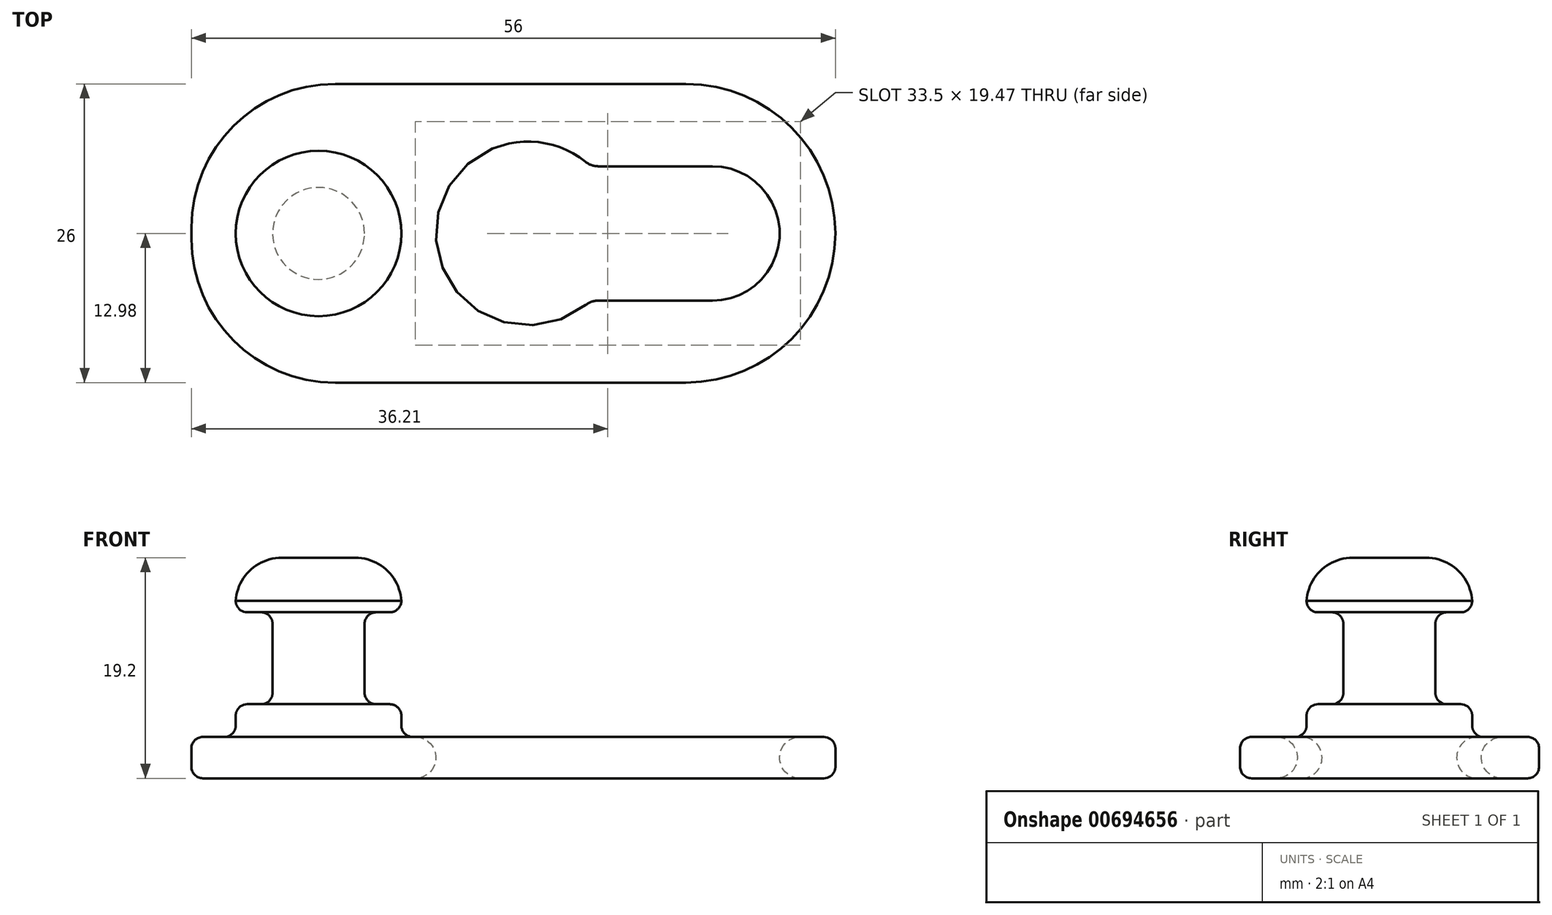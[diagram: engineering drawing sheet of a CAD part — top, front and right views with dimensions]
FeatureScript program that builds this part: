
annotation { "Feature Type Name" : "Feature", "Feature Type Description" : "" }
export const myFeature = defineFeature(function(context is Context, id is Id, definition is map)
    precondition{}
    {
        {
            var Q0;
            Q0=qCreatedBy(makeId("Top.planeOp"),FACE);
            var sketch = newSketch(context, id + "F0", { "sketchPlane" : qUnion([Q0])});
            skLineSegment(sketch, "E0", {"start": v(0, 52.84) * mm, "end": v(0, -52.67) * mm, "construction": true});
            skLineSegment(sketch, "E1", {"start": v(-57.06, 0) * mm, "end": v(21.4, 0) * mm, "construction": true});
            skLineSegment(sketch, "E2.0", {"start": v(-29.76, 0.52) * mm, "end": v(-29.76, 0) * mm});
            skLineSegment(sketch, "E3.0", {"start": v(-17.26, -12.98) * mm, "end": v(13.24, -12.98) * mm});
            skLineSegment(sketch, "E4.0", {"start": v(-17.26, 13.02) * mm, "end": v(13.24, 13.02) * mm});
            skLineSegment(sketch, "E5.0", {"start": v(5.4, 5.9) * mm, "end": v(5.4, 5.85) * mm});
            skArc(sketch, "E6", {"start": v(4.96, 5.85) * mm, "mid": v(-8.5, 0) * mm, "end": v(4.96, -5.85) * mm});
            skArc(sketch, "E7", {"start": v(15.55, -5.85) * mm, "mid": v(21.4, 0) * mm, "end": v(15.55, 5.85) * mm});
            skLineSegment(sketch, "E8", {"start": v(15.55, 5.85) * mm, "end": v(4.9, 5.85) * mm});
            skLineSegment(sketch, "E9", {"start": v(15.55, -5.85) * mm, "end": v(4.9, -5.85) * mm});
            skLineSegment(sketch, "E10.trimOffspring", {"start": v(5.4, -5.85) * mm, "end": v(5.4, -5.9) * mm});
            skPoint(sketch, "E11.0.start.orphan", {"position": v(16.05, 13) * mm});
            skPoint(sketch, "E12.trimOffspring.end.orphan", {"position": v(16.05, -13) * mm});
            skCircle(sketch, "E13", {"center": v(-18.76, 0) * mm, "radius": 7.2 * mm});
            skLineSegment(sketch, "E14", {"start": v(-11.56, 0) * mm, "end": v(-11.56, -14.31) * mm, "construction": true});
            skLineSegment(sketch, "E15", {"start": v(-25.96, 0) * mm, "end": v(-25.96, -14.7) * mm, "construction": true});
            skLineSegment(sketch, "E16", {"start": v(21.4, 0) * mm, "end": v(46.22, 0) * mm, "construction": true});
            skLineSegment(sketch, "E17", {"start": v(-8.5, 0) * mm, "end": v(-8.5, -14.52) * mm, "construction": true});
            skPoint(sketch, "E18.visualSharp", {"position": v(-29.06, 13) * mm});
            skArc(sketch, "E18.filletArc", {"start": v(-17.26, 13.02) * mm, "mid": v(-26.1, 9.36) * mm, "end": v(-29.76, 0.52) * mm});
            skArc(sketch, "E19.filletArc", {"start": v(-29.76, -0.48) * mm, "mid": v(-26.1, -9.32) * mm, "end": v(-17.26, -12.98) * mm});
            skPoint(sketch, "E20.visualSharp", {"position": v(26.94, 13) * mm});
            skArc(sketch, "E20.filletArc", {"start": v(26.24, 0.02) * mm, "mid": v(22.44, 9.21) * mm, "end": v(13.24, 13.02) * mm});
            skArc(sketch, "E21.filletArc", {"start": v(13.24, -12.98) * mm, "mid": v(22.44, -9.17) * mm, "end": v(26.24, 0.02) * mm});
            skLineSegment(sketch, "E22", {"start": v(-29.76, 0) * mm, "end": v(-29.76, -0.48) * mm});
            skSolve(sketch);
        }
        {
            var Q0;
            Q0=makeQuery(id+"F0.imprint","IMPRINT",FACE,{"disambiguationData":[TD([[makeQuery(id+"F0.imprint","IMPRINT",EDGE,{"derivedFrom":sQuery(id+"F0.wireOp",EDGE,"E2.0")}),1.0]])]});
            var Q1;
            Q1=makeQuery(id+"F0.imprint","IMPRINT",FACE,{"disambiguationData":[TD([[makeQuery(id+"F0.imprint","IMPRINT",EDGE,{"derivedFrom":sQuery(id+"F0.wireOp",EDGE,"E13")}),1.0]])]});
            extrude(context, id + "F1", {"entities" : qUnion([Q0, Q1]), "depth" : 3.6 * mm, "offsetDistance" : 25 * mm});
        }
        {
            var Q0;
            Q0=makeQuery(id+"F1.opExtrude","SWEPT_FACE",FACE,{"disambiguationData":[OSD([sQuery(id+"F0.wireOp",EDGE,"E6")])]});
            var Q1;
            Q1=makeQuery(id+"F1.opExtrude","SWEPT_FACE",FACE,{"disambiguationData":[OSD([sQuery(id+"F0.wireOp",EDGE,"E8")])]});
            var Q2;
            Q2=makeQuery(id+"F1.opExtrude","SWEPT_FACE",FACE,{"disambiguationData":[OSD([sQuery(id+"F0.wireOp",EDGE,"E7")])]});
            var Q3;
            Q3=makeQuery(id+"F1.opExtrude","SWEPT_FACE",FACE,{"disambiguationData":[OSD([sQuery(id+"F0.wireOp",EDGE,"E9")])]});
            fillet(context, id + "F2", {"entities" : qUnion([Q0, Q1, Q2, Q3]), "radius" : 1.8 * mm, "tangentPropagation" : true, "allowEdgeOverflow" : false});
        }
        {
            var Q0;
            Q0=qCreatedBy(makeId("Top.planeOp"),FACE);
            var sketch = newSketch(context, id + "F3", { "sketchPlane" : qUnion([Q0])});
            skCircle(sketch, "E23", {"center": v(-18.7, 0) * mm, "radius": 7.2 * mm});
            skSolve(sketch);
        }
        {
            var Q0;
            Q0 = qSketchRegion(id + "F3", true);
            extrude(context, id + "F4", {"entities" : qUnion([Q0]), "operationType" : NewBodyOperationType.ADD, "depth" : 6.45 * mm, "offsetDistance" : 25 * mm});
        }
        {
            var Q0;
            Q0=makeQuery(id+"F4.opExtrude","CAP_FACE",FACE,{"disambiguationData":[OSD([sQuery(id+"F3.wireOp",EDGE,"E23")])],"isStart":false});
            var sketch = newSketch(context, id + "F5", { "sketchPlane" : qUnion([Q0])});
            skCircle(sketch, "E24", {"center": v(-18.7, 0) * mm, "radius": 4 * mm});
            skSolve(sketch);
        }
        {
            var Q0;
            Q0=makeQuery(id+"F5.imprint","IMPRINT",FACE,{"disambiguationData":[TD([[makeQuery(id+"F5.imprint","IMPRINT",EDGE,{"derivedFrom":sQuery(id+"F5.wireOp",EDGE,"E24")}),1.0]])]});
            extrude(context, id + "F6", {"entities" : qUnion([Q0]), "operationType" : NewBodyOperationType.ADD, "depth" : 8 * mm, "offsetDistance" : 25 * mm});
        }
        {
            var Q0;
            Q0=makeQuery(id+"F6.opExtrude","CAP_FACE",FACE,{"disambiguationData":[OSD([sQuery(id+"F5.wireOp",EDGE,"E24")])],"isStart":false});
            var sketch = newSketch(context, id + "F7", { "sketchPlane" : qUnion([Q0])});
            skCircle(sketch, "E25", {"center": v(-18.7, 0) * mm, "radius": 7.2 * mm});
            skSolve(sketch);
        }
        {
            var Q0;
            Q0=makeQuery(id+"F4.opExtrude","CAP_FACE",FACE,{"disambiguationData":[OSD([sQuery(id+"F3.wireOp",EDGE,"E23")])],"isStart":false});
            var Q1;
            Q1=makeQuery(id+"F4.opExtrude","SWEPT_FACE",FACE,{"disambiguationData":[OSD([sQuery(id+"F3.wireOp",EDGE,"E23")])]});
            fillet(context, id + "F8", {"entities" : qUnion([Q0, Q1]), "radius" : 1 * mm, "allowEdgeOverflow" : false});
        }
        {
            var Q0;
            Q0=makeQuery(id+"F7.imprint","IMPRINT",FACE,{"disambiguationData":[TD([[makeQuery(id+"F7.imprint","IMPRINT",EDGE,{"derivedFrom":sQuery(id+"F7.wireOp",EDGE,"E25")}),1.0]])]});
            var Q1;
            Q1=makeQuery(id+"F7.imprint","IMPRINT",FACE,{"disambiguationData":[TD([[makeQuery(id+"F7.imprint","IMPRINT",EDGE,{"derivedFrom":makeQuery(id+"F6.opExtrude","CAP_EDGE",EDGE,{"disambiguationData":[OSD([sQuery(id+"F5.wireOp",EDGE,"E24")])],"isStart":false})}),1.0]])]});
            extrude(context, id + "F9", {"entities" : qUnion([Q0, Q1]), "operationType" : NewBodyOperationType.ADD, "depth" : 4.75 * mm, "offsetDistance" : 25 * mm});
        }
        {
            var Q0;
            Q0=makeQuery(id+"F9.opExtrude","CAP_FACE",FACE,{"disambiguationData":[OSD([sQuery(id+"F7.wireOp",EDGE,"E25")])],"isStart":true});
            var Q1;
            Q1=makeQuery(id+"F6.opExtrude","SWEPT_FACE",FACE,{"disambiguationData":[OSD([sQuery(id+"F5.wireOp",EDGE,"E24")])]});
            fillet(context, id + "F10", {"entities" : qUnion([Q0, Q1]), "radius" : 1 * mm, "tangentPropagation" : true, "allowEdgeOverflow" : false});
        }
        {
            var Q0;
            Q0=makeQuery(id+"F9.opExtrude","CAP_FACE",FACE,{"disambiguationData":[OSD([sQuery(id+"F7.wireOp",EDGE,"E25")])],"isStart":false});
            var Q1;
            Q1=makeQuery(id+"F9.opExtrude","SWEPT_FACE",FACE,{"disambiguationData":[OSD([sQuery(id+"F7.wireOp",EDGE,"E25")])]});
            fillet(context, id + "F11", {"entities" : qUnion([Q0, Q1]), "radius" : 4 * mm, "tangentPropagation" : true, "allowEdgeOverflow" : false});
        }
        {
            var Q0;
            Q0=makeQuery(id+"F1.opExtrude","CAP_FACE",FACE,{"disambiguationData":[OSD([sQuery(id+"F0.wireOp",EDGE,"E2.0"),sQuery(id+"F0.wireOp",EDGE,"E3.0"),sQuery(id+"F0.wireOp",EDGE,"E4.0"),sQuery(id+"F0.wireOp",EDGE,"E6"),sQuery(id+"F0.wireOp",EDGE,"E7"),sQuery(id+"F0.wireOp",EDGE,"E8"),sQuery(id+"F0.wireOp",EDGE,"E9"),sQuery(id+"F0.wireOp",EDGE,"E18.filletArc"),sQuery(id+"F0.wireOp",EDGE,"E19.filletArc"),sQuery(id+"F0.wireOp",EDGE,"E20.filletArc"),sQuery(id+"F0.wireOp",EDGE,"E21.filletArc"),sQuery(id+"F0.wireOp",EDGE,"E22")])],"isStart":false});
            var Q1;
            Q1=makeQuery(id+"F1.opExtrude","SWEPT_FACE",FACE,{"disambiguationData":[OSD([sQuery(id+"F0.wireOp",EDGE,"E19.filletArc")])]});
            var Q2;
            Q2=makeQuery(id+"F1.opExtrude","SWEPT_FACE",FACE,{"disambiguationData":[OSD([sQuery(id+"F0.wireOp",EDGE,"E3.0")])]});
            var Q3;
            Q3=makeQuery(id+"F1.opExtrude","SWEPT_FACE",FACE,{"disambiguationData":[OSD([sQuery(id+"F0.wireOp",EDGE,"E20.filletArc"),sQuery(id+"F0.wireOp",EDGE,"E21.filletArc")])]});
            var Q4;
            Q4=makeQuery(id+"F1.opExtrude","SWEPT_FACE",FACE,{"disambiguationData":[OSD([sQuery(id+"F0.wireOp",EDGE,"E4.0")])]});
            var Q5;
            Q5=makeQuery(id+"F1.opExtrude","SWEPT_FACE",FACE,{"disambiguationData":[OSD([sQuery(id+"F0.wireOp",EDGE,"E18.filletArc")])]});
            fillet(context, id + "F12", {"entities" : qUnion([Q0, Q1, Q2, Q3, Q4, Q5]), "radius" : 1 * mm, "tangentPropagation" : true, "allowEdgeOverflow" : false});
        }
    });
